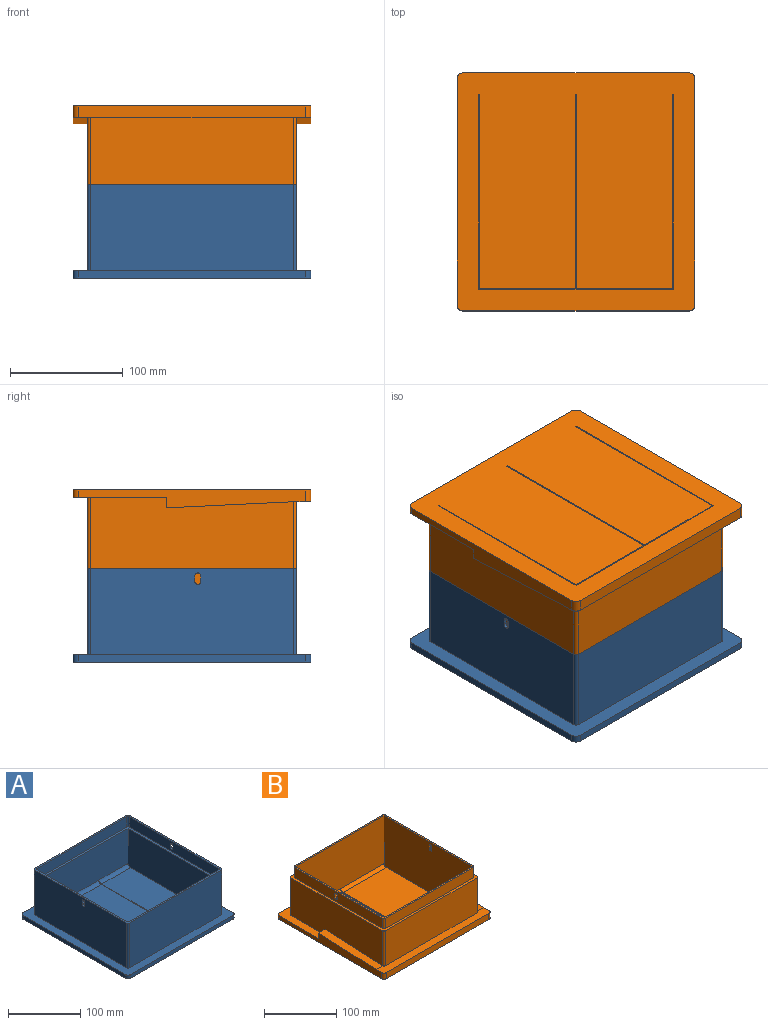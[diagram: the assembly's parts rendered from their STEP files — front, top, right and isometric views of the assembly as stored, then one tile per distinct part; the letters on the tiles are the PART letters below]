
ASSEMBLY  parts=2 mates=1
PART A: 55 faces, bbox 210.8x210.8x82.6 mm
  f0: plane 56.22x2.4mm, normal (0,-1,0), area 134.9mm2, adj f3,f23,f51,f54
  f1: plane 56.22x2.4mm, normal (0,-1,0), area 134.9mm2, adj f23,f24,f27,f52
  f2: plane 165.83x56.22mm, normal (0,0,1), area 9322.5mm2, adj f4,f25,f26,f53
  f3: plane 165.83x56.22mm, normal (0,0,1), area 9322.5mm2, adj f0,f5,f51,f54
  f4: cylinder r=6.35mm len=56.22mm, axis (-1,0,0), area 422.4mm2, adj f2,f13,f26,f53
  f5: cylinder r=6.35mm len=56.22mm, axis (-1,0,0), area 422.4mm2, adj f3,f13,f51,f54
  f6: plane 180.34x76.2mm, normal (1,0,0), area 13695.8mm2, adj f14,f29,f34,f35,f47,f48,f49,f50
  f7: plane 175.26x17.48mm, normal (-1,0,0), area 3016.6mm2, adj f35,f40,f41,f42,f47,f48,f49,f50
  f8: plane 180.34x76.2mm, normal (-1,0,0), area 13695.8mm2, adj f14,f31,f32,f35,f43,f44,f45,f46
  f9: plane 175.26x17.48mm, normal (1,0,0), area 3016.6mm2, adj f35,f37,f38,f42,f43,f44,f45,f46
  f10: plane 172.72x65.08mm, normal (-1,0,0), area 11239.7mm2, adj f11,f13,f23,f42
  f11: plane 172.72x65.08mm, normal (0,1,0), area 11239.7mm2, adj f10,f12,f23,f42
  f12: plane 172.72x65.08mm, normal (1,0,0), area 11239.7mm2, adj f11,f13,f23,f42
  f13: plane 172.72x65.08mm, normal (0,-1,0), area 10168.8mm2, adj f4,f5,f10,f12,f23,f24,f26,f28
  f14: plane 210.82x210.82mm, normal (0,0,1), area 10047.9mm2, adj f6,f8,f15,f16,f17,f18,f19,f20
  f15: plane 200.66x6.35mm, normal (1,0,0), area 1274.2mm2, adj f14,f16,f22,f23
  f16: cylinder r=5.08mm len=6.35mm, axis (0,0,-1), area 50.7mm2, adj f14,f15,f17,f23
  f17: plane 200.66x6.35mm, normal (0,1,0), area 1274.2mm2, adj f14,f16,f18,f23
  f18: cylinder r=5.08mm len=6.35mm, axis (0,0,-1), area 50.7mm2, adj f14,f17,f19,f23
  f19: plane 200.66x6.35mm, normal (-1,0,0), area 1274.2mm2, adj f14,f18,f20,f23
  f20: cylinder r=5.08mm len=6.35mm, axis (0,0,-1), area 50.7mm2, adj f14,f19,f21,f23
  f21: plane 200.66x6.35mm, normal (0,-1,0), area 1274.2mm2, adj f14,f20,f22,f23
  f22: cylinder r=5.08mm len=6.35mm, axis (0,0,-1), area 50.7mm2, adj f14,f15,f21,f23
  f23: plane 210.82x210.82mm, normal (0,0,-1), area 43549.6mm2, adj f0,f1,f10,f11,f12,f13,f15,f16
  f24: plane 171.7x6.35mm, normal (-1,0,0), area 418.5mm2, adj f1,f13,f23,f27,f28
  f25: plane 56.22x2.4mm, normal (0,-1,0), area 134.9mm2, adj f2,f23,f26,f53
  f26: plane 171.7x6.35mm, normal (1,0,0), area 418.5mm2, adj f2,f4,f13,f23,f25
  f27: plane 165.83x56.22mm, normal (0,0,1), area 9322.5mm2, adj f1,f24,f28,f52
  f28: cylinder r=6.35mm len=56.22mm, axis (-1,0,0), area 422.4mm2, adj f13,f24,f27,f52
  f29: cylinder r=2.54mm len=76.2mm, axis (0,0,-1), area 304mm2, adj f6,f14,f30,f35
  f30: plane 180.34x76.2mm, normal (0,1,0), area 13741.9mm2, adj f14,f29,f31,f35
  f31: cylinder r=2.54mm len=76.2mm, axis (0,0,-1), area 304mm2, adj f8,f14,f30,f35
  f32: cylinder r=2.54mm len=76.2mm, axis (0,0,-1), area 304mm2, adj f8,f14,f33,f35
  f33: plane 180.34x76.2mm, normal (0,-1,0), area 13741.9mm2, adj f14,f32,f34,f35
  f34: cylinder r=2.54mm len=76.2mm, axis (0,0,-1), area 304mm2, adj f6,f14,f33,f35
  f35: plane 185.42x185.42mm, normal (0,0,1), area 1858.1mm2, adj f6,f7,f8,f9,f29,f30,f31,f32
  f36: plane 175.26x17.48mm, normal (0,-1,0), area 3062.7mm2, adj f35,f37,f41,f42
  f37: cylinder r=2.54mm len=17.48mm, axis (0,0,1), area 69.7mm2, adj f9,f35,f36,f42
  f38: cylinder r=2.54mm len=17.48mm, axis (0,0,1), area 69.7mm2, adj f9,f35,f39,f42
  f39: plane 175.26x17.48mm, normal (0,1,0), area 3062.7mm2, adj f35,f38,f40,f42
  f40: cylinder r=2.54mm len=17.48mm, axis (0,0,1), area 69.7mm2, adj f7,f35,f39,f42
  f41: cylinder r=2.54mm len=17.48mm, axis (0,0,1), area 69.7mm2, adj f7,f35,f36,f42
  f42: plane 180.34x180.34mm, normal (0,0,1), area 2684.8mm2, adj f7,f9,f10,f11,f12,f13,f36,f37
  f43: plane 5.08x2.54mm, normal (0,1,0), area 12.9mm2, adj f8,f9,f44,f46
  f44: cylinder r=2.54mm len=5.08mm, axis (-1,0,0), area 20.3mm2, adj f8,f9,f43,f45
  f45: plane 5.08x2.54mm, normal (0,-1,0), area 12.9mm2, adj f8,f9,f44,f46
  f46: cylinder r=2.54mm len=5.08mm, axis (-1,0,0), area 20.3mm2, adj f8,f9,f43,f45
  f47: plane 5.08x2.54mm, normal (0,-1,0), area 12.9mm2, adj f6,f7,f48,f50
  f48: cylinder r=2.54mm len=5.08mm, axis (1,0,0), area 20.3mm2, adj f6,f7,f47,f49
  f49: plane 5.08x2.54mm, normal (0,1,0), area 12.9mm2, adj f6,f7,f48,f50
  f50: cylinder r=2.54mm len=5.08mm, axis (1,0,0), area 20.3mm2, adj f6,f7,f47,f49
  f51: plane 171.7x6.35mm, normal (-1,0,0), area 418.5mm2, adj f0,f3,f5,f13,f23
  f52: plane 171.7x6.35mm, normal (1,0,0), area 418.5mm2, adj f1,f13,f23,f27,f28
  f53: plane 171.7x6.35mm, normal (-1,0,0), area 418.5mm2, adj f2,f4,f13,f23,f25
  f54: plane 171.7x6.35mm, normal (1,0,0), area 418.5mm2, adj f0,f3,f5,f13,f23
PART B: 55 faces, bbox 210.8x210.8x87.3 mm
  f0: plane 210.82x82.55mm, normal (0,0,1), area 4443.3mm2, adj f1,f9,f10,f12,f13,f17,f18,f19
  f1: plane 180.34x63.5mm, normal (1,0,0), area 10687.9mm2, adj f0,f12,f15,f39,f50,f51
  f2: plane 84.84x3mm, normal (0,-1,0), area 254.5mm2, adj f27,f28,f31,f49
  f3: plane 166.11x84.84mm, normal (0,0,1), area 14091.9mm2, adj f4,f29,f30,f48
  f4: cylinder r=6.35mm len=84.84mm, axis (-1,0,0), area 581.1mm2, adj f3,f25,f30,f48
  f5: plane 172.72x87.33mm, normal (-1,0,0), area 15036.7mm2, adj f16,f24,f25,f27,f44,f45,f46,f47
  f6: plane 172.72x17.48mm, normal (1,0,0), area 2972.2mm2, adj f16,f35,f36,f39,f44,f45,f46,f47
  f7: plane 172.72x87.33mm, normal (1,0,0), area 15036.7mm2, adj f16,f24,f25,f27,f40,f41,f42,f43
  f8: plane 172.72x17.48mm, normal (-1,0,0), area 2972.2mm2, adj f16,f33,f38,f39,f40,f41,f42,f43
  f9: plane 180.34x63.5mm, normal (0,1,0), area 11451.6mm2, adj f0,f12,f13,f39
  f10: plane 180.34x63.5mm, normal (-1,0,0), area 10687.9mm2, adj f0,f13,f14,f39,f53,f54
  f11: plane 180.34x59.44mm, normal (0,-1,0), area 10718.7mm2, adj f14,f15,f39,f52
  f12: cylinder r=2.54mm len=63.5mm, axis (0,0,-1), area 253.4mm2, adj f0,f1,f9,f39
  f13: cylinder r=2.54mm len=63.5mm, axis (0,0,-1), area 253.4mm2, adj f0,f9,f10,f39
  f14: cylinder r=2.54mm len=59.44mm, axis (0,0,-1), area 237.1mm2, adj f10,f11,f39,f52
  f15: cylinder r=2.54mm len=59.44mm, axis (0,0,-1), area 237.1mm2, adj f1,f11,f39,f52
  f16: plane 177.8x177.8mm, normal (0,0,1), area 1775.1mm2, adj f5,f6,f7,f8,f24,f25,f33,f34
  f17: plane 200.66x15.8mm, normal (1,0,0), area 2079.2mm2, adj f0,f18,f26,f27,f50,f51,f52
  f18: cylinder r=5.08mm len=6.35mm, axis (0,0,-1), area 50.7mm2, adj f0,f17,f19,f27
  f19: plane 200.66x6.35mm, normal (0,1,0), area 1274.2mm2, adj f0,f18,f20,f27
  f20: cylinder r=5.08mm len=6.35mm, axis (0,0,-1), area 50.7mm2, adj f0,f19,f21,f27
  f21: plane 200.66x15.8mm, normal (-1,0,0), area 2079.2mm2, adj f0,f20,f22,f27,f52,f53,f54
  f22: cylinder r=5.08mm len=10.41mm, axis (0,0,-1), area 83.1mm2, adj f21,f23,f27,f52
  f23: plane 200.66x10.41mm, normal (0,-1,0), area 2089.7mm2, adj f22,f26,f27,f52
  f24: plane 172.72x87.33mm, normal (0,1,0), area 15082.8mm2, adj f5,f7,f16,f27
  f25: plane 172.72x87.33mm, normal (0,-1,0), area 14005.4mm2, adj f4,f5,f7,f16,f27,f28,f30,f32
  f26: cylinder r=5.08mm len=10.41mm, axis (0,0,-1), area 83.1mm2, adj f17,f23,f27,f52
  f27: plane 210.82x210.82mm, normal (0,0,-1), area 43724.1mm2, adj f2,f5,f7,f17,f18,f19,f20,f21
  f28: plane 171.7x6.35mm, normal (-1,0,0), area 520.5mm2, adj f2,f25,f27,f31,f32
  f29: plane 84.84x3mm, normal (0,-1,0), area 254.5mm2, adj f3,f27,f30,f48
  f30: plane 171.7x6.35mm, normal (1,0,0), area 520.5mm2, adj f3,f4,f25,f27,f29
  f31: plane 166.11x84.84mm, normal (0,0,1), area 14091.9mm2, adj f2,f28,f32,f49
  f32: cylinder r=6.35mm len=84.84mm, axis (-1,0,0), area 581.1mm2, adj f25,f28,f31,f49
  f33: cylinder r=2.54mm len=17.48mm, axis (0,0,1), area 69.7mm2, adj f8,f16,f34,f39
  f34: plane 172.72x17.48mm, normal (0,1,0), area 3018.3mm2, adj f16,f33,f35,f39
  f35: cylinder r=2.54mm len=17.48mm, axis (0,0,1), area 69.7mm2, adj f6,f16,f34,f39
  f36: cylinder r=2.54mm len=17.48mm, axis (0,0,1), area 69.7mm2, adj f6,f16,f37,f39
  f37: plane 172.72x17.48mm, normal (0,-1,0), area 3018.3mm2, adj f16,f36,f38,f39
  f38: cylinder r=2.54mm len=17.48mm, axis (0,0,1), area 69.7mm2, adj f8,f16,f37,f39
  f39: plane 185.42x185.42mm, normal (0,0,1), area 2767.7mm2, adj f1,f6,f8,f9,f10,f11,f12,f13
  f40: plane 5.08x2.54mm, normal (0,1,0), area 12.9mm2, adj f7,f8,f41,f43
  f41: cylinder r=2.54mm len=5.08mm, axis (-1,0,0), area 20.3mm2, adj f7,f8,f40,f42
  f42: plane 5.08x2.54mm, normal (0,-1,0), area 12.9mm2, adj f7,f8,f41,f43
  f43: cylinder r=2.54mm len=5.08mm, axis (-1,0,0), area 20.3mm2, adj f7,f8,f40,f42
  f44: plane 5.08x2.54mm, normal (0,-1,0), area 12.9mm2, adj f5,f6,f45,f47
  f45: cylinder r=2.54mm len=5.08mm, axis (1,0,0), area 20.3mm2, adj f5,f6,f44,f46
  f46: plane 5.08x2.54mm, normal (0,1,0), area 12.9mm2, adj f5,f6,f45,f47
  f47: cylinder r=2.54mm len=5.08mm, axis (1,0,0), area 20.3mm2, adj f5,f6,f44,f46
  f48: plane 171.7x6.35mm, normal (-1,0,0), area 520.5mm2, adj f3,f4,f25,f27,f29
  f49: plane 171.7x6.35mm, normal (1,0,0), area 520.5mm2, adj f2,f25,f27,f31,f32
  f50: plane 12.7x9.45mm, normal (0,1,0), area 120mm2, adj f0,f1,f17,f51
  f51: plane 113.03x12.7mm, normal (0,-0.05,1), area 1437.1mm2, adj f1,f17,f50,f52
  f52: plane 210.82x15.24mm, normal (0,0,1), area 2733.6mm2, adj f11,f14,f15,f17,f21,f22,f23,f26
  f53: plane 12.7x9.45mm, normal (0,1,0), area 120mm2, adj f0,f10,f21,f54
  f54: plane 113.03x12.7mm, normal (0,-0.05,1), area 1437.1mm2, adj f10,f21,f52,f53
PLACE A at identity fixed
PLACE B rot(axis=(0,1,0),180deg) t=(0,0,152.4)mm
MATE fastened B.f13 <-> A.f29  axis (0,0,-1) through (90.17,90.17,82.55)mm
